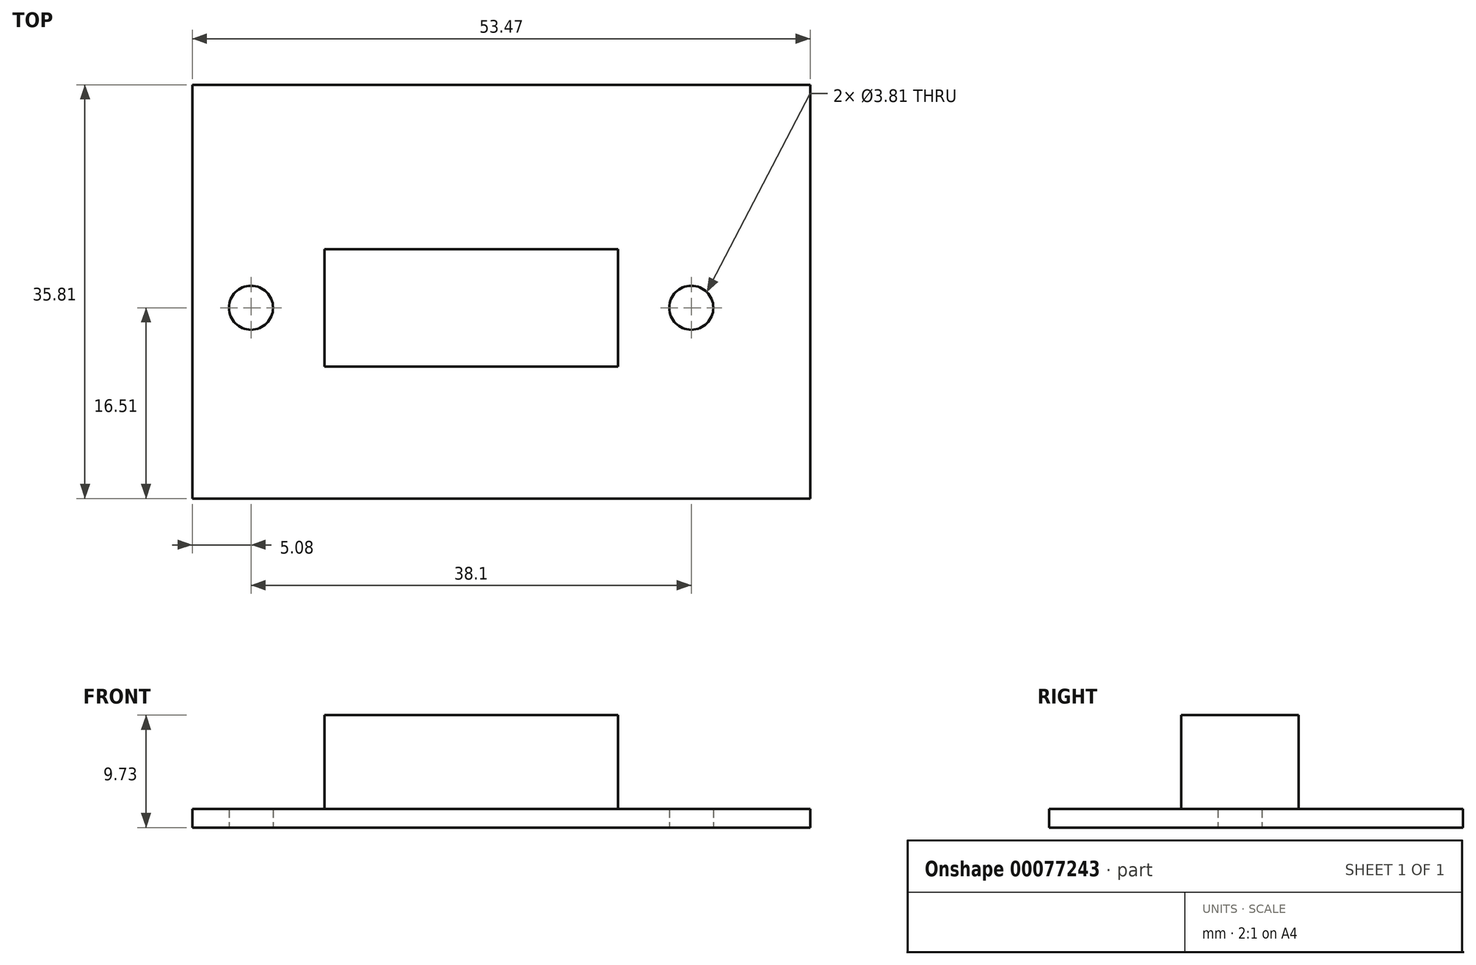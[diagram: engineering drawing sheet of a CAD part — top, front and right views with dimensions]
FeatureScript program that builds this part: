
annotation { "Feature Type Name" : "Feature", "Feature Type Description" : "" }
export const myFeature = defineFeature(function(context is Context, id is Id, definition is map)
    precondition{}
    {
        {
            var Q0;
            Q0=qCreatedBy(makeId("Top.planeOp"),FACE);
            var sketch = newSketch(context, id + "F0", { "sketchPlane" : qUnion([Q0])});
            skLineSegment(sketch, "E0.bottom", {"start": v(-24.13, -16.51) * mm, "end": v(29.34, -16.51) * mm});
            skLineSegment(sketch, "E0.top", {"start": v(-24.13, 19.3) * mm, "end": v(29.34, 19.3) * mm});
            skLineSegment(sketch, "E0.left", {"start": v(-24.13, -16.51) * mm, "end": v(-24.13, 19.3) * mm});
            skLineSegment(sketch, "E0.right", {"start": v(29.34, -16.51) * mm, "end": v(29.34, 19.3) * mm});
            skCircle(sketch, "E1", {"center": v(-19.05, 0) * mm, "radius": 1.9 * mm});
            skLineSegment(sketch, "E2", {"start": v(-19.05, 0) * mm, "end": v(19.05, 0) * mm, "construction": true});
            skCircle(sketch, "E3", {"center": v(19.05, 0) * mm, "radius": 1.9 * mm});
            skSolve(sketch);
        }
        {
            var Q0;
            Q0=qSketchRegion(id+"F0",true);
            extrude(context, id + "F1", {"entities" : qUnion([Q0]), "depth" : 1.6 * mm});
        }
        {
            var Q0;
            Q0=makeQuery(id+"F1.opExtrude","CAP_FACE",FACE,{"disambiguationData":[OSD([sQuery(id+"F0.wireOp",EDGE,"E0.bottom"),sQuery(id+"F0.wireOp",EDGE,"E0.top"),sQuery(id+"F0.wireOp",EDGE,"E0.left"),sQuery(id+"F0.wireOp",EDGE,"E0.right"),sQuery(id+"F0.wireOp",EDGE,"E1"),sQuery(id+"F0.wireOp",EDGE,"E3")])],"isStart":false});
            var sketch = newSketch(context, id + "F2", { "sketchPlane" : qUnion([Q0])});
            skLineSegment(sketch, "E4.bottom", {"start": v(-12.7, 5.08) * mm, "end": v(12.7, 5.08) * mm});
            skLineSegment(sketch, "E4.top", {"start": v(-12.7, -5.08) * mm, "end": v(12.7, -5.08) * mm});
            skLineSegment(sketch, "E4.left", {"start": v(-12.7, 5.08) * mm, "end": v(-12.7, -5.08) * mm});
            skLineSegment(sketch, "E4.right", {"start": v(12.7, 5.08) * mm, "end": v(12.7, -5.08) * mm});
            skLineSegment(sketch, "E5", {"start": v(-12.7, 0) * mm, "end": v(-19.05, 0) * mm, "construction": true});
            skSolve(sketch);
        }
        {
            var Q0;
            Q0=qSketchRegion(id+"F2",true);
            extrude(context, id + "F3", {"entities" : qUnion([Q0]), "operationType" : NewBodyOperationType.ADD, "depth" : 8.13 * mm});
        }
    });
